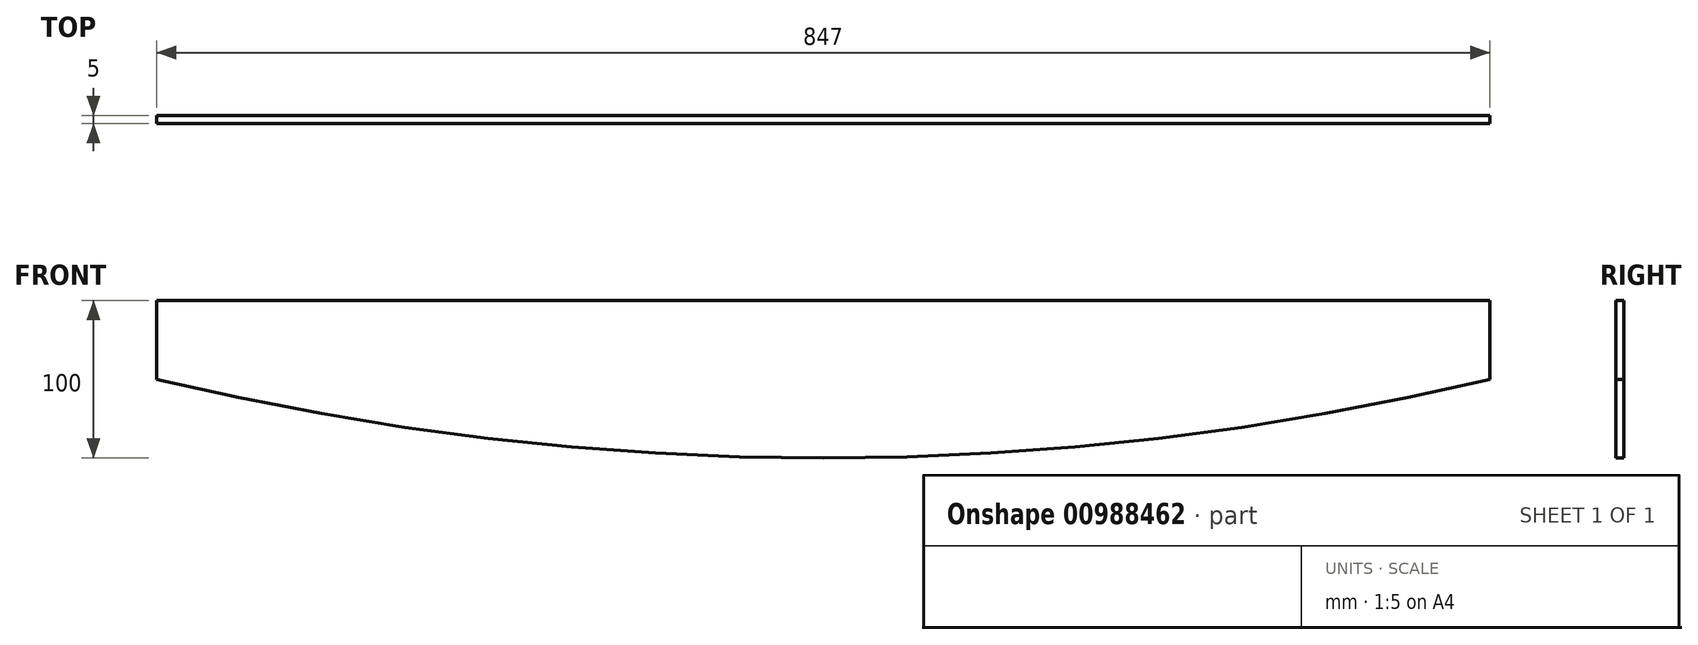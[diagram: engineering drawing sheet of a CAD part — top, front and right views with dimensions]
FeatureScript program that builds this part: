
annotation { "Feature Type Name" : "Feature", "Feature Type Description" : "" }
export const myFeature = defineFeature(function(context is Context, id is Id, definition is map)
    precondition{}
    {
        {
            var Q0;
            Q0=qCreatedBy(makeId("Front.planeOp"),FACE);
            var sketch = newSketch(context, id + "F0", { "sketchPlane" : qUnion([Q0])});
            skLineSegment(sketch, "E0.bottom", {"start": v(423.5, -50) * mm, "end": v(-423.5, -50) * mm});
            skLineSegment(sketch, "E0.top", {"start": v(423.5, 50) * mm, "end": v(-423.5, 50) * mm});
            skLineSegment(sketch, "E0.left", {"start": v(423.5, -50) * mm, "end": v(423.5, 50) * mm});
            skLineSegment(sketch, "E0.right", {"start": v(-423.5, -50) * mm, "end": v(-423.5, 50) * mm});
            skPoint(sketch, "E0.middle", {"position": v(0, 0) * mm});
            skPoint(sketch, "E1.third.point", {"position": v(0, -50) * mm});
            skArc(sketch, "E2", {"start": v(-423.5, 0) * mm, "mid": v(0, -50) * mm, "end": v(423.5, 0) * mm});
            skPoint(sketch, "E2.first.point", {"position": v(-423.5, 0) * mm});
            skPoint(sketch, "E2.third.point", {"position": v(423.5, 0) * mm});
            skSolve(sketch);
        }
        {
            var Q0;
            {var subQ1=sQuery(id+"F0.wireOp",EDGE,"E0.top");Q0=makeQuery(id+"F0.imprint","IMPRINT",FACE,{"disambiguationData":[TD([[makeQuery(id+"F0.imprint","IMPRINT",EDGE,{"derivedFrom":subQ1}),1.0]])]});}
            extrude(context, id + "F1", {"entities" : qUnion([Q0]), "depth" : 5 * mm, "offsetDistance" : 25 * mm});
        }
    });
